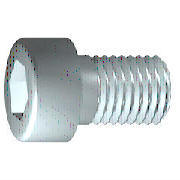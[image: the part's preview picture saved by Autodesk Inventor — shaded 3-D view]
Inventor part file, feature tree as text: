
AUTODESK INVENTOR PART (.ipt)
format: ipt  version: 2022 (Build 260153000, 153)  size: 196,096 bytes
history: native  units: mm (DEFAULTED — no unit token found)
features: sketch x2, other x1, extrude x1, plane x1, fillet x1
ambient origin geometry x7: Origin, YZ Plane, XY Plane, X Axis, Y Axis, Z Axis, Center Point
bodies: Solid1 (feature_tree)
feature tree (6):
  other  "Cuerpo"
  extrude  "Ranura"  Depth=2.0mm
  plane  "Work Plane1"
  fillet  "Fillet2"  Radius=2.0mm
  sketch  "Boceto1"  dims[d1=4.0mm d2=0.24548mm d3=2.0mm]
  sketch  "Boceto2"  dims[d4=1.0mm d5=60.0deg d6=2.0mm d7=2.0mm d8=1.732051mm d9=3.8mm d10=90.0deg d11=10.0mm d12=0.0mm d13=4.0mm d14=0.0mm d15=0.24538mm d16=0.24538mm d17=0.2mm d19=0.0mm d26=5.0mm d27=45.0deg d28=0.0mm d29=0.0mm d30=0.1mm]
